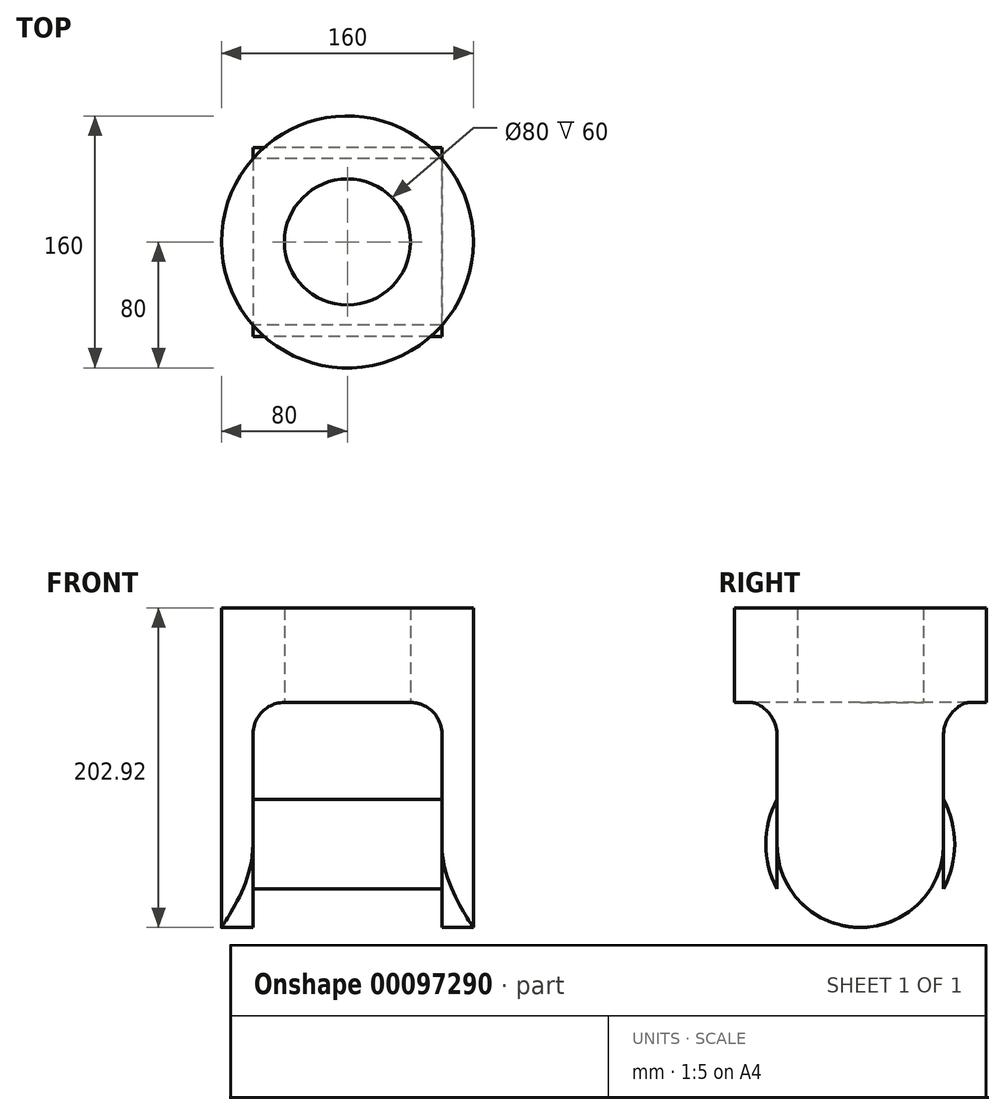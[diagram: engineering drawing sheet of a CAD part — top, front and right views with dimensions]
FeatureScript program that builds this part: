
annotation { "Feature Type Name" : "Feature", "Feature Type Description" : "" }
export const myFeature = defineFeature(function(context is Context, id is Id, definition is map)
    precondition{}
    {
        {
            var Q0;
            Q0=qCreatedBy(makeId("Top.planeOp"),FACE);
            var sketch = newSketch(context, id + "F8", { "sketchPlane" : qUnion([Q0])});
            skCircle(sketch, "E0", {"center": v(0, 0) * mm, "radius": 40 * mm});
            skCircle(sketch, "E1", {"center": v(0, 0) * mm, "radius": 80 * mm});
            skSolve(sketch);
        }
        {
            var Q0;
            Q0=makeQuery(id+"F8.imprint","IMPRINT",FACE,{"disambiguationData":[TD([[makeQuery(id+"F8.imprint","IMPRINT",EDGE,{"derivedFrom":sQuery(id+"F8.wireOp",EDGE,"E0")}),1.0]])]});
            extrude(context, id + "F9", {"entities" : qUnion([Q0]), "endBound" : BoundingType.SYMMETRIC, "depth" : 120 * mm});
        }
        {
            var Q0;
            Q0=qCreatedBy(makeId("Right.planeOp"),FACE);
            var sketch = newSketch(context, id + "F0", { "sketchPlane" : qUnion([Q0])});
            skCircle(sketch, "E2", {"center": v(0, 0) * mm, "radius": 60 * mm});
            skCircle(sketch, "E3", {"center": v(0, 0) * mm, "radius": 5 * mm});
            skCircle(sketch, "E4", {"center": v(0, 0) * mm, "radius": 9 * mm});
            skSolve(sketch);
        }
        {
            var Q0;
            Q0=makeQuery(id+"F0.imprint","IMPRINT",FACE,{"disambiguationData":[TD([[makeQuery(id+"F0.imprint","IMPRINT",EDGE,{"derivedFrom":sQuery(id+"F0.wireOp",EDGE,"E3")}),-1.0]])]});
            var Q1;
            Q1=makeQuery(id+"F0.imprint","IMPRINT",FACE,{"disambiguationData":[TD([[makeQuery(id+"F0.imprint","IMPRINT",EDGE,{"derivedFrom":sQuery(id+"F0.wireOp",EDGE,"E2")}),1.0]])]});
            extrude(context, id + "F1", {"entities" : qUnion([Q0, Q1]), "endBound" : BoundingType.SYMMETRIC, "depth" : 120 * mm});
        }
        {
            var Q0;
            Q0=makeQuery(id+"F9.opExtrude","SWEPT_BODY",BODY,{"disambiguationData":[OSD([sQuery(id+"F8.wireOp",EDGE,"E0")])]});
            var Q1;
            Q1=makeQuery(id+"F1.opExtrude","SWEPT_BODY",BODY,{"disambiguationData":[OSD([sQuery(id+"F0.wireOp",EDGE,"E2"),sQuery(id+"F0.wireOp",EDGE,"E3")])]});
            booleanBodies(context, id + "F2", {"operationType" : BooleanOperationType.SUBTRACTION, "tools" : qUnion([Q0]), "targets" : qUnion([Q1])});
        }
        {
            var Q0;
            Q0=makeQuery(id+"F0.imprint","IMPRINT",FACE,{"disambiguationData":[TD([[makeQuery(id+"F0.imprint","IMPRINT",EDGE,{"derivedFrom":sQuery(id+"F0.wireOp",EDGE,"E3")}),-1.0]])]});
            extrude(context, id + "F10", {"entities" : qUnion([Q0]), "operationType" : NewBodyOperationType.REMOVE, "endBound" : BoundingType.SYMMETRIC, "oppositeDirection" : true, "depth" : 90 * mm});
        }
        {
            var Q0;
            Q0=makeQuery(id+"F8.imprint","IMPRINT",FACE,{"disambiguationData":[TD([[makeQuery(id+"F8.imprint","IMPRINT",EDGE,{"derivedFrom":sQuery(id+"F8.wireOp",EDGE,"E0")}),-1.0]])]});
            extrude(context, id + "F3", {"entities" : qUnion([Q0]), "depth" : 150 * mm, "hasSecondDirection" : true, "secondDirectionOppositeDirection" : true, "secondDirectionDepth" : 60 * mm});
        }
        {
            var Q0;
            Q0=makeQuery(id+"F1.opExtrude","CAP_FACE",FACE,{"disambiguationData":[OSD([sQuery(id+"F0.wireOp",EDGE,"E2"),sQuery(id+"F0.wireOp",EDGE,"E3")])],"isStart":false});
            var sketch = newSketch(context, id + "F4", { "sketchPlane" : qUnion([Q0])});
            skCircle(sketch, "E5", {"center": v(0, 0) * mm, "radius": 52.92 * mm});
            skLineSegment(sketch, "E6.bottom", {"start": v(-52.92, 0) * mm, "end": v(52.92, 0) * mm});
            skLineSegment(sketch, "E6.top", {"start": v(-52.92, 120) * mm, "end": v(52.92, 120) * mm});
            skLineSegment(sketch, "E6.left", {"start": v(-52.92, 0) * mm, "end": v(-52.92, 120) * mm});
            skLineSegment(sketch, "E6.right", {"start": v(52.92, 0) * mm, "end": v(52.92, 120) * mm});
            skLineSegment(sketch, "E7.bottom", {"start": v(-90, 150) * mm, "end": v(90, 150) * mm});
            skLineSegment(sketch, "E7.top", {"start": v(-90, 90) * mm, "end": v(90, 90) * mm});
            skLineSegment(sketch, "E7.left", {"start": v(-90, 150) * mm, "end": v(-90, 90) * mm});
            skLineSegment(sketch, "E7.right", {"start": v(90, 150) * mm, "end": v(90, 90) * mm});
            skPoint(sketch, "E7.middle", {"position": v(0, 120) * mm});
            skSolve(sketch);
        }
        {
            var Q0;
            Q0 = qSketchRegion(id + "F4", true);
            extrude(context, id + "F11", {"entities" : qUnion([Q0]), "depth" : 25 * mm, "hasSecondDirection" : true, "secondDirectionOppositeDirection" : true, "secondDirectionDepth" : 145 * mm});
        }
        {
            var Q0;
            Q0=makeQuery(id+"F3.opExtrude","SWEPT_BODY",BODY,{"disambiguationData":[OSD([sQuery(id+"F8.wireOp",EDGE,"E0"),sQuery(id+"F8.wireOp",EDGE,"E1")])]});
            var Q1;
            Q1=makeQuery(id+"F11.opExtrude","SWEPT_BODY",BODY,{"disambiguationData":[OSD([sQuery(id+"F4.wireOp",EDGE,"E5"),sQuery(id+"F4.wireOp",EDGE,"E6.left"),sQuery(id+"F4.wireOp",EDGE,"E6.right"),sQuery(id+"F4.wireOp",EDGE,"E7.bottom"),sQuery(id+"F4.wireOp",EDGE,"E7.top"),sQuery(id+"F4.wireOp",EDGE,"E7.left"),sQuery(id+"F4.wireOp",EDGE,"E7.right")])]});
            booleanBodies(context, id + "F5", {"operationType" : BooleanOperationType.INTERSECTION, "tools" : qUnion([Q0, Q1])});
        }
        {
            var Q0;
            Q0=makeQuery(id+"F11.opExtrude","SWEPT_FACE",FACE,{"disambiguationData":[OSD([sQuery(id+"F4.wireOp",EDGE,"E6.left")])]});
            var sketch = newSketch(context, id + "F6", { "sketchPlane" : qUnion([Q0])});
            skLineSegment(sketch, "E8.bottom", {"start": v(-60, 90) * mm, "end": v(60, 90) * mm});
            skLineSegment(sketch, "E8.top", {"start": v(-60, -60) * mm, "end": v(60, -60) * mm});
            skLineSegment(sketch, "E8.left", {"start": v(-60, 90) * mm, "end": v(-60, -60) * mm});
            skLineSegment(sketch, "E8.right", {"start": v(60, 90) * mm, "end": v(60, -60) * mm});
            skSolve(sketch);
        }
        {
            var Q0;
            Q0 = qSketchRegion(id + "F6", true);
            var Q1;
            Q1=makeQuery(id+"F11.opExtrude","SWEPT_FACE",FACE,{"disambiguationData":[OSD([sQuery(id+"F4.wireOp",EDGE,"E6.right")])]});
            extrude(context, id + "F7", {"entities" : qUnion([Q0]), "operationType" : NewBodyOperationType.REMOVE, "endBound" : BoundingType.UP_TO_SURFACE, "oppositeDirection" : true, "endBoundEntityFace" : qUnion([Q1]), "depth" : 25 * mm});
        }
        {
            var Q0;
            Q0=makeQuery(id+"F7.boolean.opBoolean","COPY",EDGE,{"derivedFrom":makeQuery(id+"F7.opExtrude","SWEPT_EDGE",EDGE,{"disambiguationData":[OSD([sQuery(id+"F6.wireOp",EDGE,"E8.bottom"),sQuery(id+"F6.wireOp",EDGE,"E8.left")])]})});
            var Q1;
            Q1=makeQuery(id+"F7.boolean.opBoolean","COPY",EDGE,{"derivedFrom":makeQuery(id+"F7.opExtrude","SWEPT_EDGE",EDGE,{"disambiguationData":[OSD([sQuery(id+"F6.wireOp",EDGE,"E8.bottom"),sQuery(id+"F6.wireOp",EDGE,"E8.right")])]})});
            fillet(context, id + "F12", {"entities" : qUnion([Q0, Q1]), "radius" : 20 * mm, "tangentPropagation" : true, "allowEdgeOverflow" : false});
        }
    });
